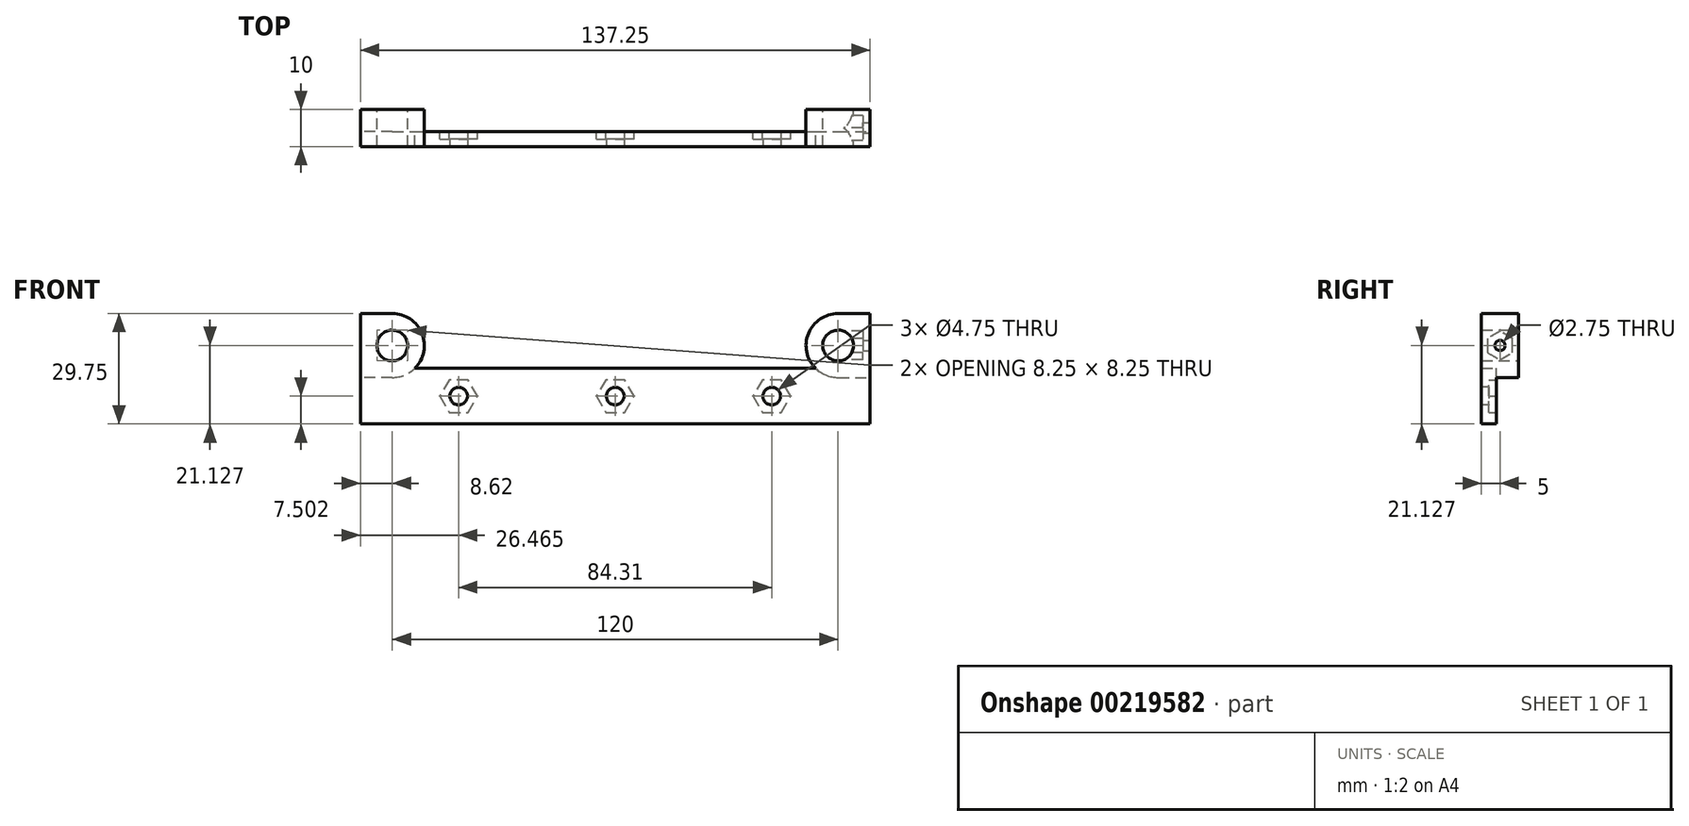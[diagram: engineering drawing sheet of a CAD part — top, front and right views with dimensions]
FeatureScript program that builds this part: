
annotation { "Feature Type Name" : "Feature", "Feature Type Description" : "" }
export const myFeature = defineFeature(function(context is Context, id is Id, definition is map)
    precondition{}
    {
        {
            var Q0;
            Q0=qCreatedBy(makeId("Front.planeOp"),FACE);
            var sketch = newSketch(context, id + "F0", { "sketchPlane" : qUnion([Q0])});
            skCircle(sketch, "E0", {"center": v(-60, 34.35) * mm, "radius": 4.12 * mm});
            skCircle(sketch, "E1", {"center": v(60, 34.35) * mm, "radius": 4.12 * mm});
            skCircle(sketch, "E2", {"center": v(-60, 34.35) * mm, "radius": 8.62 * mm});
            skCircle(sketch, "E3", {"center": v(60, 34.35) * mm, "radius": 8.62 * mm});
            skLineSegment(sketch, "E4.bottom", {"start": v(-60, 38.47) * mm, "end": v(-64.12, 38.47) * mm});
            skLineSegment(sketch, "E4.top", {"start": v(-60, 30.22) * mm, "end": v(-64.12, 30.22) * mm});
            skLineSegment(sketch, "E4.left", {"start": v(-60, 38.47) * mm, "end": v(-60, 30.22) * mm});
            skLineSegment(sketch, "E4.right", {"start": v(-64.12, 38.47) * mm, "end": v(-64.12, 30.22) * mm});
            skLineSegment(sketch, "E5.bottom", {"start": v(60, 38.47) * mm, "end": v(64.12, 38.47) * mm});
            skLineSegment(sketch, "E5.top", {"start": v(60, 30.22) * mm, "end": v(64.12, 30.22) * mm});
            skLineSegment(sketch, "E5.left", {"start": v(60, 38.47) * mm, "end": v(60, 30.22) * mm});
            skLineSegment(sketch, "E5.right", {"start": v(64.12, 38.47) * mm, "end": v(64.12, 30.22) * mm});
            skLineSegment(sketch, "E6.bottom", {"start": v(-60, 42.97) * mm, "end": v(-68.62, 42.97) * mm});
            skLineSegment(sketch, "E6.top", {"start": v(-60, 25.72) * mm, "end": v(-68.62, 25.72) * mm});
            skLineSegment(sketch, "E6.left", {"start": v(-60, 42.97) * mm, "end": v(-60, 25.72) * mm});
            skLineSegment(sketch, "E6.right", {"start": v(-68.62, 42.97) * mm, "end": v(-68.62, 25.72) * mm});
            skLineSegment(sketch, "E7.bottom", {"start": v(60, 42.97) * mm, "end": v(68.62, 42.97) * mm});
            skLineSegment(sketch, "E7.top", {"start": v(60, 25.72) * mm, "end": v(68.62, 25.72) * mm});
            skLineSegment(sketch, "E7.left", {"start": v(60, 42.97) * mm, "end": v(60, 25.72) * mm});
            skLineSegment(sketch, "E7.right", {"start": v(68.62, 42.97) * mm, "end": v(68.62, 25.72) * mm});
            skSolve(sketch);
        }
        {
            var Q0;
            Q0 = qSketchRegion(id + "F0", true);
            extrude(context, id + "F1", {"entities" : qUnion([Q0]), "depth" : 5 * mm, "hasSecondDirection" : true, "secondDirectionOppositeDirection" : true, "secondDirectionDepth" : 5 * mm});
        }
        {
            var Q0;
            Q0=makeQuery(id+"F1.opExtrude","CAP_FACE",FACE,{"disambiguationData":[OSD([sQuery(id+"F0.wireOp",EDGE,"E0"),sQuery(id+"F0.wireOp",EDGE,"E2"),sQuery(id+"F0.wireOp",EDGE,"E4.bottom"),sQuery(id+"F0.wireOp",EDGE,"E4.top"),sQuery(id+"F0.wireOp",EDGE,"E4.right"),sQuery(id+"F0.wireOp",EDGE,"E6.bottom"),sQuery(id+"F0.wireOp",EDGE,"E6.top"),sQuery(id+"F0.wireOp",EDGE,"E6.right")])],"isStart":false});
            var sketch = newSketch(context, id + "F2", { "sketchPlane" : qUnion([Q0])});
            skLineSegment(sketch, "E8.bottom", {"start": v(-68.62, 13.22) * mm, "end": v(68.62, 13.22) * mm});
            skLineSegment(sketch, "E8.top", {"start": v(-68.62, 28.22) * mm, "end": v(68.62, 28.22) * mm});
            skLineSegment(sketch, "E8.left", {"start": v(-68.62, 13.22) * mm, "end": v(-68.62, 28.22) * mm});
            skLineSegment(sketch, "E8.right", {"start": v(68.62, 13.22) * mm, "end": v(68.62, 28.22) * mm});
            skSolve(sketch);
        }
        {
            var Q0;
            Q0 = qSketchRegion(id + "F2", true);
            var Q1;
            Q1=makeQuery(id+"F1.opExtrude","CAP_FACE",FACE,{"disambiguationData":[OSD([sQuery(id+"F0.wireOp",EDGE,"E1"),sQuery(id+"F0.wireOp",EDGE,"E3")])],"isStart":true});
            extrude(context, id + "F3", {"entities" : qUnion([Q0]), "operationType" : NewBodyOperationType.ADD, "oppositeDirection" : true, "endBoundEntityFace" : qUnion([Q1]), "depth" : 4 * mm});
        }
        {
            var Q0;
            Q0=makeQuery(id+"F3.opExtrude","CAP_FACE",FACE,{"disambiguationData":[OSD([sQuery(id+"F2.wireOp",EDGE,"E8.bottom"),sQuery(id+"F2.wireOp",EDGE,"E8.top"),sQuery(id+"F2.wireOp",EDGE,"E8.left"),sQuery(id+"F2.wireOp",EDGE,"E8.right")])],"isStart":true});
            var sketch = newSketch(context, id + "F4", { "sketchPlane" : qUnion([Q0])});
            skCircle(sketch, "E9", {"center": v(0, 20.72) * mm, "radius": 2.38 * mm});
            skCircle(sketch, "E10", {"center": v(42.16, 20.72) * mm, "radius": 2.38 * mm});
            skCircle(sketch, "E11", {"center": v(-42.16, 20.72) * mm, "radius": 2.38 * mm});
            skLineSegment(sketch, "E12", {"start": v(0, 28.22) * mm, "end": v(0, 20.72) * mm, "construction": true});
            skLineSegment(sketch, "E13", {"start": v(0, 20.72) * mm, "end": v(0, 13.22) * mm, "construction": true});
            skSolve(sketch);
        }
        {
            var Q0;
            Q0 = qSketchRegion(id + "F4", true);
            extrude(context, id + "F5", {"entities" : qUnion([Q0]), "operationType" : NewBodyOperationType.REMOVE, "endBound" : BoundingType.THROUGH_ALL, "oppositeDirection" : true, "depth" : 25 * mm});
        }
        {
            var Q0;
            Q0=makeQuery(id+"F3.opExtrude","CAP_FACE",FACE,{"disambiguationData":[OSD([sQuery(id+"F2.wireOp",EDGE,"E8.bottom"),sQuery(id+"F2.wireOp",EDGE,"E8.top"),sQuery(id+"F2.wireOp",EDGE,"E8.left"),sQuery(id+"F2.wireOp",EDGE,"E8.right")])],"isStart":false});
            var sketch = newSketch(context, id + "F6", { "sketchPlane" : qUnion([Q0])});
            skCircle(sketch, "E14.cCircle", {"center": v(0, 20.72) * mm, "radius": 4.4 * mm, "construction": true});
            skLineSegment(sketch, "E14.0", {"start": v(-2.54, 25.12) * mm, "end": v(2.54, 25.12) * mm});
            skLineSegment(sketch, "E14.1", {"start": v(2.54, 25.12) * mm, "end": v(5.08, 20.72) * mm});
            skLineSegment(sketch, "E14.2", {"start": v(5.08, 20.72) * mm, "end": v(2.54, 16.32) * mm});
            skLineSegment(sketch, "E14.3", {"start": v(2.54, 16.32) * mm, "end": v(-2.54, 16.32) * mm});
            skLineSegment(sketch, "E14.4", {"start": v(-2.54, 16.32) * mm, "end": v(-5.08, 20.72) * mm});
            skLineSegment(sketch, "E14.5", {"start": v(-5.08, 20.72) * mm, "end": v(-2.54, 25.12) * mm});
            skPoint(sketch, "E14.0.midPoint", {"position": v(0, 25.12) * mm});
            skCircle(sketch, "E15.cCircle", {"center": v(-42.16, 20.72) * mm, "radius": 4.4 * mm, "construction": true});
            skLineSegment(sketch, "E15.0", {"start": v(-44.7, 25.12) * mm, "end": v(-39.61, 25.12) * mm});
            skLineSegment(sketch, "E15.1", {"start": v(-39.61, 25.12) * mm, "end": v(-37.07, 20.72) * mm});
            skLineSegment(sketch, "E15.2", {"start": v(-37.07, 20.72) * mm, "end": v(-39.61, 16.32) * mm});
            skLineSegment(sketch, "E15.3", {"start": v(-39.61, 16.32) * mm, "end": v(-44.7, 16.32) * mm});
            skLineSegment(sketch, "E15.4", {"start": v(-44.7, 16.32) * mm, "end": v(-47.24, 20.72) * mm});
            skLineSegment(sketch, "E15.5", {"start": v(-47.24, 20.72) * mm, "end": v(-44.7, 25.12) * mm});
            skPoint(sketch, "E15.0.midPoint", {"position": v(-42.16, 25.12) * mm});
            skLineSegment(sketch, "E16", {"start": v(-42.16, 20.72) * mm, "end": v(0, 20.72) * mm, "construction": true});
            skLineSegment(sketch, "E17", {"start": v(0, 20.72) * mm, "end": v(-42.16, 20.72) * mm, "construction": true});
            skCircle(sketch, "E18.cCircle", {"center": v(42.16, 20.72) * mm, "radius": 4.4 * mm, "construction": true});
            skLineSegment(sketch, "E18.0", {"start": v(39.61, 25.12) * mm, "end": v(44.7, 25.12) * mm});
            skLineSegment(sketch, "E18.1", {"start": v(44.7, 25.12) * mm, "end": v(47.24, 20.72) * mm});
            skLineSegment(sketch, "E18.2", {"start": v(47.24, 20.72) * mm, "end": v(44.7, 16.32) * mm});
            skLineSegment(sketch, "E18.3", {"start": v(44.7, 16.32) * mm, "end": v(39.61, 16.32) * mm});
            skLineSegment(sketch, "E18.4", {"start": v(39.61, 16.32) * mm, "end": v(37.07, 20.72) * mm});
            skLineSegment(sketch, "E18.5", {"start": v(37.07, 20.72) * mm, "end": v(39.61, 25.12) * mm});
            skPoint(sketch, "E18.0.midPoint", {"position": v(42.16, 25.12) * mm});
            skLineSegment(sketch, "E19", {"start": v(0, 20.72) * mm, "end": v(42.16, 20.72) * mm, "construction": true});
            skSolve(sketch);
        }
        {
            var Q0;
            Q0 = qSketchRegion(id + "F6", true);
            extrude(context, id + "F7", {"entities" : qUnion([Q0]), "operationType" : NewBodyOperationType.REMOVE, "oppositeDirection" : true, "depth" : 2 * mm});
        }
        {
            var Q0;
            Q0=makeQuery(id+"F3.opExtrude","SWEPT_FACE",FACE,{"disambiguationData":[OSD([sQuery(id+"F2.wireOp",EDGE,"E8.right")])]});
            var sketch = newSketch(context, id + "F8", { "sketchPlane" : qUnion([Q0])});
            skCircle(sketch, "E20", {"center": v(0, 34.35) * mm, "radius": 1.38 * mm});
            skLineSegment(sketch, "E21.0.0", {"start": v(5, 38.47) * mm, "end": v(5, 30.22) * mm, "construction": true});
            skLineSegment(sketch, "E21.0.1", {"start": v(5, 30.22) * mm, "end": v(-5, 30.22) * mm, "construction": true});
            skLineSegment(sketch, "E21.0.2", {"start": v(-5, 30.22) * mm, "end": v(-5, 38.47) * mm, "construction": true});
            skLineSegment(sketch, "E21.0.3", {"start": v(-5, 38.47) * mm, "end": v(5, 38.47) * mm, "construction": true});
            skPoint(sketch, "E22", {"position": v(5, 34.35) * mm});
            skSolve(sketch);
        }
        {
            var Q0;
            Q0 = qSketchRegion(id + "F8", true);
            extrude(context, id + "F9", {"entities" : qUnion([Q0]), "operationType" : NewBodyOperationType.REMOVE, "endBound" : BoundingType.UP_TO_NEXT, "oppositeDirection" : true, "depth" : 25 * mm});
        }
        {
            var Q0;
            Q0=makeQuery(id+"F1.opExtrude","SWEPT_FACE",FACE,{"disambiguationData":[OSD([sQuery(id+"F0.wireOp",EDGE,"E5.right")])]});
            var sketch = newSketch(context, id + "F10", { "sketchPlane" : qUnion([Q0])});
            skCircle(sketch, "E23.cCircle", {"center": v(0, 34.35) * mm, "radius": 3.35 * mm, "construction": true});
            skLineSegment(sketch, "E23.0", {"start": v(3.35, 36.28) * mm, "end": v(3.35, 32.41) * mm});
            skLineSegment(sketch, "E23.1", {"start": v(3.35, 32.41) * mm, "end": v(0, 30.48) * mm});
            skLineSegment(sketch, "E23.2", {"start": v(0, 30.48) * mm, "end": v(-3.35, 32.41) * mm});
            skLineSegment(sketch, "E23.3", {"start": v(-3.35, 32.41) * mm, "end": v(-3.35, 36.28) * mm});
            skLineSegment(sketch, "E23.4", {"start": v(-3.35, 36.28) * mm, "end": v(0, 38.22) * mm});
            skLineSegment(sketch, "E23.5", {"start": v(0, 38.22) * mm, "end": v(3.35, 36.28) * mm});
            skPoint(sketch, "E23.0.midPoint", {"position": v(3.35, 34.35) * mm});
            skSolve(sketch);
        }
        {
            var Q0;
            Q0 = qSketchRegion(id + "F10", true);
            extrude(context, id + "F11", {"entities" : qUnion([Q0]), "operationType" : NewBodyOperationType.REMOVE, "oppositeDirection" : true, "depth" : 2.5 * mm});
        }
        {
            var Q0;
            Q0=makeQuery(id+"F1.opExtrude","SWEPT_EDGE",EDGE,{"disambiguationData":[OSD([sQuery(id+"F0.wireOp",EDGE,"E5.bottom"),sQuery(id+"F0.wireOp",EDGE,"E5.right")])]});
            var Q1;
            Q1=makeQuery(id+"F1.opExtrude","SWEPT_EDGE",EDGE,{"disambiguationData":[OSD([sQuery(id+"F0.wireOp",EDGE,"E5.top"),sQuery(id+"F0.wireOp",EDGE,"E5.right")])]});
            var Q2;
            Q2=makeQuery(id+"F1.opExtrude","SWEPT_EDGE",EDGE,{"disambiguationData":[OSD([sQuery(id+"F0.wireOp",EDGE,"E4.bottom"),sQuery(id+"F0.wireOp",EDGE,"E4.right")])]});
            var Q3;
            Q3=makeQuery(id+"F1.opExtrude","SWEPT_EDGE",EDGE,{"disambiguationData":[OSD([sQuery(id+"F0.wireOp",EDGE,"E4.top"),sQuery(id+"F0.wireOp",EDGE,"E4.right")])]});
            fillet(context, id + "F12", {"entities" : qUnion([Q0, Q1, Q2, Q3]), "radius" : 4 * mm, "tangentPropagation" : true, "allowEdgeOverflow" : false});
        }
    });
